# Revit family: cekchionnie_protivopozarnie_vorota_firetecnics_ei60
name_source: partatom
category: Двери
revit_build: Autodesk Revit 2018 (Build: 20170223_1515(x64)
units: mm (PartAtom-declared; Revit-internal decimal feet)

## family parameters
Всегда вертикально = Да
Заголовок OmniClass = Doors
Номер OmniClass = 23.30.10.00
Общий = Нет
Основа = Стена
При загрузке вырезать с полостями = Нет
Точка расчета площади = Нет

## types (1)
- Секционные противопожарные ворота FireTechnics EI60
    ADSK_URL страницы изделия = https://www.fire-tec.ru
    ADSK_Завод-изготовитель = Firetechnics
    ADSK_Наименование = Секционные противопожарные ворота FireTechnics EI60
    ADSK_Предел огнестойкости = EI60
    ADSK_Размер_Высота = 3000 мм
    ADSK_Размер_Ширина = 3000 мм
    URL = https://www.fire-tec.ru
    Аналитическая конструкция = <Нет>
    Высота = 3000 мм
    Высота двери = 2000 мм
    Высота лючка = 200 мм
    Высота мотора = 500 мм
    Глубина выступа = 40 мм
    Диаметр втулки = 20 мм
    Длина направляющей = 76 мм
    Замыкание стены = По основе
    Изготовитель = Firetechnics
    Крепеж на стену = 250 мм
    Материал направляющих = Сталь_оцинкованная_листовая
    Материал полотна = Firetech полотно
    Огнестойкость = EI60
    Функция = Внутренние слои
    Ширина = 3000 мм
    Ширина верхней направляющей = 3600 мм
    Ширина двери = 1000 мм
    Ширина люка = 200 мм
    Ширина направляющих = 100 мм
    Ширина полотна = 60 мм
    высота верхней направляющей = 200 мм
    дальняя точка мотора = 450 мм

## geometry (parser evidence)
native form markers: Blend x4
no freeform markers — native parametric forms only
